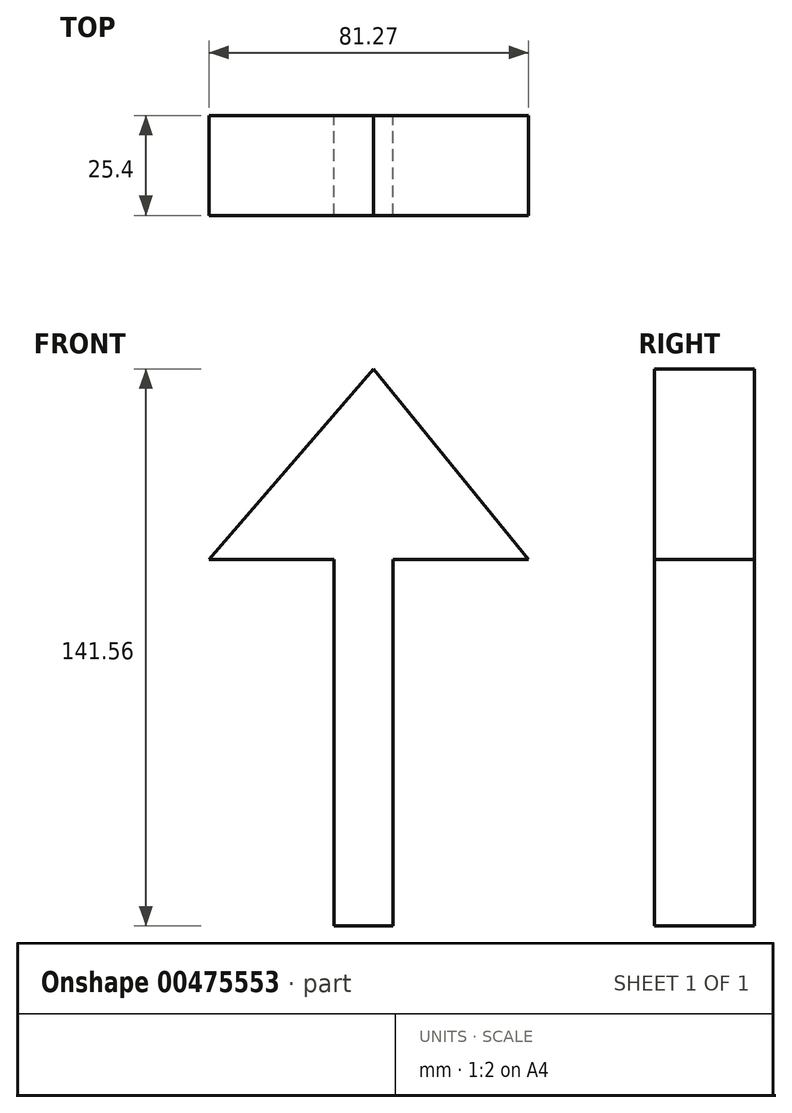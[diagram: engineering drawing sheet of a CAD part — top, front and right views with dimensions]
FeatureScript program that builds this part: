
annotation { "Feature Type Name" : "Feature", "Feature Type Description" : "" }
export const myFeature = defineFeature(function(context is Context, id is Id, definition is map)
    precondition{}
    {
        {
            var Q0;
            Q0=qCreatedBy(makeId("Front.planeOp"),FACE);
            var sketch = newSketch(context, id + "F0", { "sketchPlane" : qUnion([Q0])});
            skLineSegment(sketch, "E0", {"start": v(0, 73.02) * mm, "end": v(-44.48, 21.54) * mm});
            skLineSegment(sketch, "E1", {"start": v(0, 73.02) * mm, "end": v(39.45, 24.62) * mm});
            skLineSegment(sketch, "E2", {"start": v(39.45, 24.62) * mm, "end": v(5.04, 24.62) * mm});
            skLineSegment(sketch, "E3", {"start": v(-10.07, 24.62) * mm, "end": v(-10.07, -68.54) * mm});
            skLineSegment(sketch, "E4", {"start": v(-10.07, -68.54) * mm, "end": v(5.04, -68.54) * mm});
            skLineSegment(sketch, "E5", {"start": v(5.04, -68.54) * mm, "end": v(5.04, 24.62) * mm});
            skLineSegment(sketch, "E6.trimOffspring", {"start": v(-10.07, 24.62) * mm, "end": v(-41.82, 24.62) * mm});
            skSolve(sketch);
        }
        {
            var Q0;
            {var subQ0=sQuery(id+"F0.wireOp",EDGE,"E1");Q0=makeQuery(id+"F0.imprint","IMPRINT",FACE,{"disambiguationData":[TD([[makeQuery(id+"F0.imprint","IMPRINT",EDGE,{"derivedFrom":subQ0}),-1.0]])]});}
            extrude(context, id + "F1", {"entities" : qUnion([Q0]), "depth" : 25.4 * mm});
        }
    });
